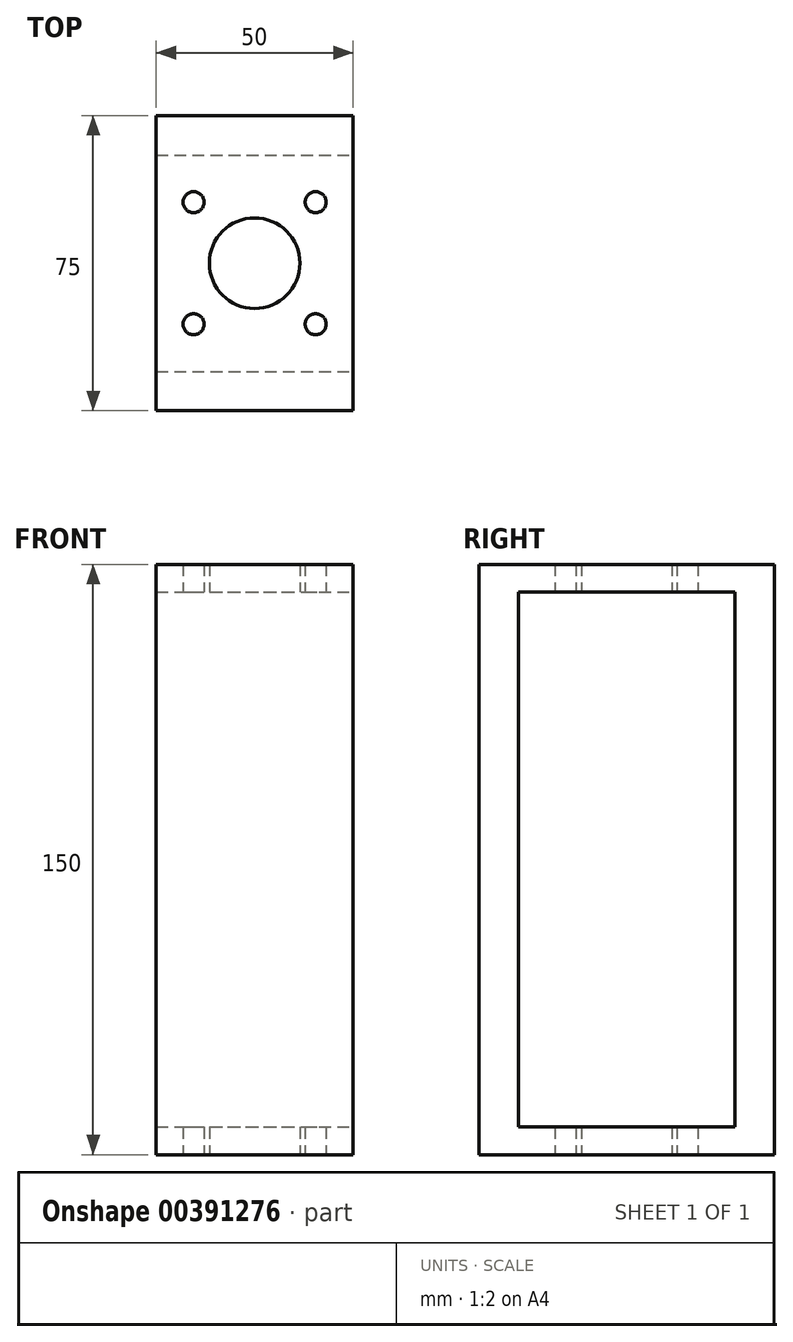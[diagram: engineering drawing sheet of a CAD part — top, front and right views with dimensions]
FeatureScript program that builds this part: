
annotation { "Feature Type Name" : "Feature", "Feature Type Description" : "" }
export const myFeature = defineFeature(function(context is Context, id is Id, definition is map)
    precondition{}
    {
        {
            var Q0;
            Q0=qCreatedBy(makeId("Top.planeOp"),FACE);
            var sketch = newSketch(context, id + "F0", { "sketchPlane" : qUnion([Q0])});
            skLineSegment(sketch, "E0.bottom", {"start": v(15.5, -15.5) * mm, "end": v(-15.5, -15.5) * mm, "construction": true});
            skLineSegment(sketch, "E0.top", {"start": v(15.5, 15.5) * mm, "end": v(-15.5, 15.5) * mm, "construction": true});
            skLineSegment(sketch, "E0.left", {"start": v(15.5, -15.5) * mm, "end": v(15.5, 15.5) * mm, "construction": true});
            skLineSegment(sketch, "E0.right", {"start": v(-15.5, -15.5) * mm, "end": v(-15.5, 15.5) * mm, "construction": true});
            skPoint(sketch, "E0.middle", {"position": v(0, 0) * mm});
            skCircle(sketch, "E1", {"center": v(0, 0) * mm, "radius": 11.5 * mm});
            skCircle(sketch, "E2", {"center": v(-15.5, 15.5) * mm, "radius": 2.67 * mm});
            skCircle(sketch, "E3.MirrorC", {"center": v(15.5, 15.5) * mm, "radius": 2.67 * mm});
            skCircle(sketch, "E4.MirrorC", {"center": v(-15.5, -15.5) * mm, "radius": 2.67 * mm});
            skCircle(sketch, "E5.MirrorC", {"center": v(15.5, -15.5) * mm, "radius": 2.67 * mm});
            skLineSegment(sketch, "E6.bottom", {"start": v(25, -37.5) * mm, "end": v(-25, -37.5) * mm});
            skLineSegment(sketch, "E6.top", {"start": v(25, 37.5) * mm, "end": v(-25, 37.5) * mm});
            skLineSegment(sketch, "E6.left", {"start": v(25, -37.5) * mm, "end": v(25, 37.5) * mm});
            skLineSegment(sketch, "E6.right", {"start": v(-25, -37.5) * mm, "end": v(-25, 37.5) * mm});
            skSolve(sketch);
        }
        {
            var Q0;
            Q0=makeQuery(id+"F0.imprint","IMPRINT",FACE,{"disambiguationData":[TD([[makeQuery(id+"F0.imprint","IMPRINT",EDGE,{"derivedFrom":sQuery(id+"F0.wireOp",EDGE,"E1")}),-1.0]])]});
            extrude(context, id + "F1", {"entities" : qUnion([Q0]), "depth" : 150 * mm});
        }
        {
            var Q0;
            Q0=qCreatedBy(makeId("Right.planeOp"),FACE);
            var sketch = newSketch(context, id + "F2", { "sketchPlane" : qUnion([Q0])});
            skLineSegment(sketch, "E7.bottom", {"start": v(-27.5, 143) * mm, "end": v(27.5, 143) * mm});
            skLineSegment(sketch, "E7.top", {"start": v(-27.5, 7) * mm, "end": v(27.5, 7) * mm});
            skLineSegment(sketch, "E7.left", {"start": v(-27.5, 143) * mm, "end": v(-27.5, 7) * mm});
            skLineSegment(sketch, "E7.right", {"start": v(27.5, 143) * mm, "end": v(27.5, 7) * mm});
            skSolve(sketch);
        }
        {
            var Q0;
            Q0=makeQuery(id+"F2.imprint","IMPRINT",FACE,{"disambiguationData":[TD([[makeQuery(id+"F2.imprint","IMPRINT",EDGE,{"derivedFrom":sQuery(id+"F2.wireOp",EDGE,"E7.bottom")}),-1.0]])]});
            extrude(context, id + "F3", {"entities" : qUnion([Q0]), "operationType" : NewBodyOperationType.REMOVE, "oppositeDirection" : true, "depth" : 50 * mm, "hasSecondDirection" : true, "secondDirectionOppositeDirection" : false, "secondDirectionDepth" : 50 * mm});
        }
    });
